# Revit family: NBS_Allermuir_DmstcChrs_Mote_Ottoman
name_source: partatom
category: Furniture
revit_build: Autodesk Revit 2016 (Build: 20161004_0715(x64)
units: mm (PartAtom-declared; Revit-internal decimal feet)

## family parameters
Always vertical = Yes
Cut with Voids When Loaded = No
Room Calculation Point = No
Shared = No
Work Plane-Based = No

## types (3) — shared parameters
AssetType = Moveable
Category = Pr_40_50_12_22:Dining chairs
Depth = 750 mm  [stored 2.46063 ft]
DurationUnit = year
ExpectedLife = 5
FrameColourOptions = Flint grey, mineral sand, mellow yellow, orange crush
FrameHeight = 246 mm  [stored 0.807087 ft]
FrameMountingMaterial = NBS_Concept
FramesColour = Black
FramesFinish = Powder coat
FramesMaterial = Aluminium
IfcExportAs = IfcFurnitureType
IfcExportType = SOFA
IsBuiltIn = No
ManufacturerName = Allermuir
ManufacturerURL = http://www.thesenatorgroup.com
ModelReference = Mote ottoman
NBSCertification = www.nationalbimlibrary.com/cert/uof10nxk
NBSDescription = Domestic chairs
NBSReference = 45-35-20/365
NominalDepth = 1000 mm  [stored 3.28084 ft]
NominalHeight = 470 mm
NominalLength = 730 mm
NominalWidth = 1000 mm  [stored 3.28084 ft]
ProductInformation = http://www.thesenatorgroup.com
SeatArmRestHeight = 604 mm  [stored 1.98163 ft]
SeatEndRestOffset = 65 mm  [stored 0.213255 ft]
SeatFrameMaterial = NBS_Concept
SeatFrameWidth = 50 mm  [stored 0.164042 ft]
SeatLegOffset = 165 mm
SeatPowerSupplyMaterial = NBS_Concept
SeatScreenHeight = 1325 mm  [stored 4.34711 ft]
SeatingArmRestMaterial = NBS_Concept
SeatingSeatMaterial = NBS_Concept
SeatsAndBacksFinish = Two-tone upholstery available
SeatsAndBacksMaterial = Upholstered
SingleSeatWidth = 1045 mm  [stored 3.42848 ft]
Status = UNSET
ThreeSeatWidth = 2245 mm  [stored 7.36549 ft]
TwoSeatWidth = 1645 mm
Uniclass2015Code = Pr_40_50_12_22
Uniclass2015Title = Dining chairs
Uniclass2015Version = Products v1.9
Version = 1
WarrantyDescription = Allermuir warrant that its manufactured products are free from manufacturing defects in materials or workmanship for a period of five years
WarrantyDurationParts = 5
WarrantyDurationUnit = year
zero-valued in all types: HighestSeatingHeight, LowestSeatingHeight

## per-type parameters (varying)
| type | BIMObjectName | Description | Features | IsSingleSeat | IsThreeSeat | IsTwoSeat | LeftSeatPositionOffset | Name | OptionalAccessories | RightSeatPositionWidth | SeatOverallWidth | SeatingHeight | ShowMultipleSeat |
| MTE-OT01 | NBS_Allermuir_DomesticChairs_Mote_MTE-OT01 | Single seat ottoman | Fully upholstered, cast aluminium legs and aluminium perimeter frame finished in black powder coat, plastic glides with leveling adjustment, aluminium frame available in flint grey, mineral sand, mellow yellow or orange crush powder coat, two-tone upholstery | Yes | No | No | 0 mm  [stored 0 ft] | DomesticChairs_Mote_MTE-OT01_Allermuir | 1 x front facing frame intergrated power unit with 2 x powered USB and 1 x power socket, 1 x rear facing frame intergrated power unit with 2 x powered USB and 1 x power socket | 400 mm  [stored 1.31234 ft] | 1045 mm  [stored 3.42848 ft] | 468 mm  [stored 1.53543 ft] | No |
| MTE-OT02 | NBS_Allermuir_DomesticChairs_Mote_MTE-OT02 | Two seat ottoman | Fully upholstered, cast aluminium legs and aluminium perimeter frame finished in black powder coat, plastic glides with leveling adjustment, aluminium frame available in flint grey, mineral sand, mellow yellow or orange crush powder coat, end arms, single arm mid, two-tone upholstery | No | No | Yes | 0 mm  [stored 0 ft] | DomesticChairs_Mote_MTE-OT02_Allermuir | 1 x front facing frame intergrated power unit with 2 x powered USB and 1 x power socket, 1 x rear facing, frame intergrated power unit with 2 x powered USB and 1 x power socket | 400 mm  [stored 1.31234 ft] | 1645 mm | 468 mm  [stored 1.53543 ft] | Yes |
| MTE-OT03 | NBS_Allermuir_DomesticChairs_Mote_MTE-OT03 | Three seat ottoman | Fully upholstered, cast aluminium legs and aluminium perimeter frame finished in black powder coat, plastic glides with leveling adjustment, aluminium frame available in flint grey, mineral sand, mellow yellow or orange crush powder coat, end arms,double arms intermediate, two-tone upholstery | No | Yes | No | 400 mm  [stored 1.31234 ft] | DomesticChairs_Mote_MTE-OT03_Allermuir | 2 x front facing frame intergrated power unit with 2 x powered USB and 1 x power socket, 2 x rear facing, frame intergrated power unit with 2 x powered USB and 1 x power socket | 800 mm  [stored 2.62467 ft] | 2245 mm  [stored 7.36549 ft] | 470 mm | Yes |

note: column(s) folded — value = type name in every type: ModelNumber

note: [stored X ft] marks values corroborated as IEEE doubles in the binary element streams (Revit-internal decimal feet)

## geometry (parser evidence)
native form markers: Sweep x12
no freeform markers — native parametric forms only
